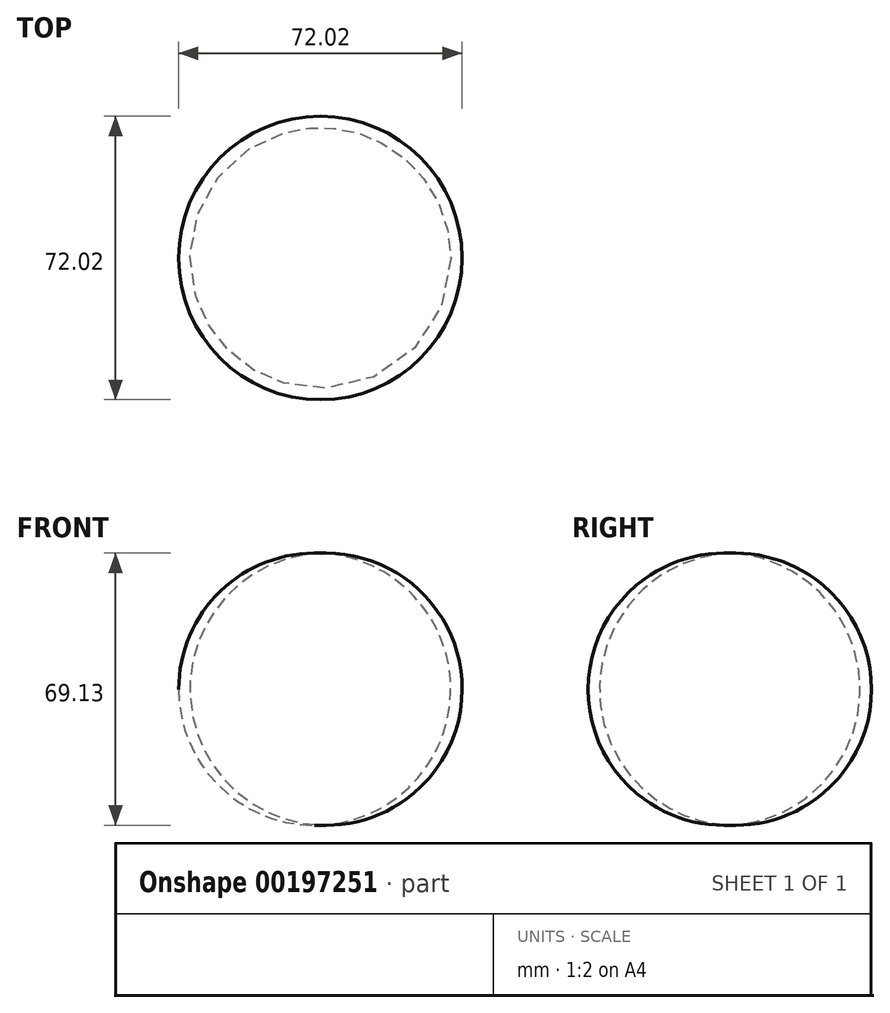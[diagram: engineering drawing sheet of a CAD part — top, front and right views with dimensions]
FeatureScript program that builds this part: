
annotation { "Feature Type Name" : "Feature", "Feature Type Description" : "" }
export const myFeature = defineFeature(function(context is Context, id is Id, definition is map)
    precondition{}
    {
        {
            var Q0;
            Q0=qCreatedBy(makeId("Front.planeOp"),FACE);
            var sketch = newSketch(context, id + "F0", { "sketchPlane" : qUnion([Q0])});
            skLineSegment(sketch, "E0", {"start": v(0, 0) * mm, "end": v(0, 69.07) * mm});
            skArc(sketch, "E1", {"start": v(0, 69.07) * mm, "mid": v(-36, 34.54) * mm, "end": v(0, 0) * mm});
            skSolve(sketch);
        }
        {
            var Q0;
            Q0=makeQuery(id+"F0.imprint","IMPRINT",FACE,{"disambiguationData":[TD([[makeQuery(id+"F0.imprint","IMPRINT",EDGE,{"derivedFrom":sQuery(id+"F0.wireOp",EDGE,"E0")}),1.0]])]});
            var Q1;
            Q1=sQuery(id+"F0.wireOp",EDGE,"E0");
            revolve(context, id + "F1", {"entities" : qUnion([Q0]), "axis" : qUnion([Q1]), "revolveType" : RevolveType.FULL});
        }
    });
